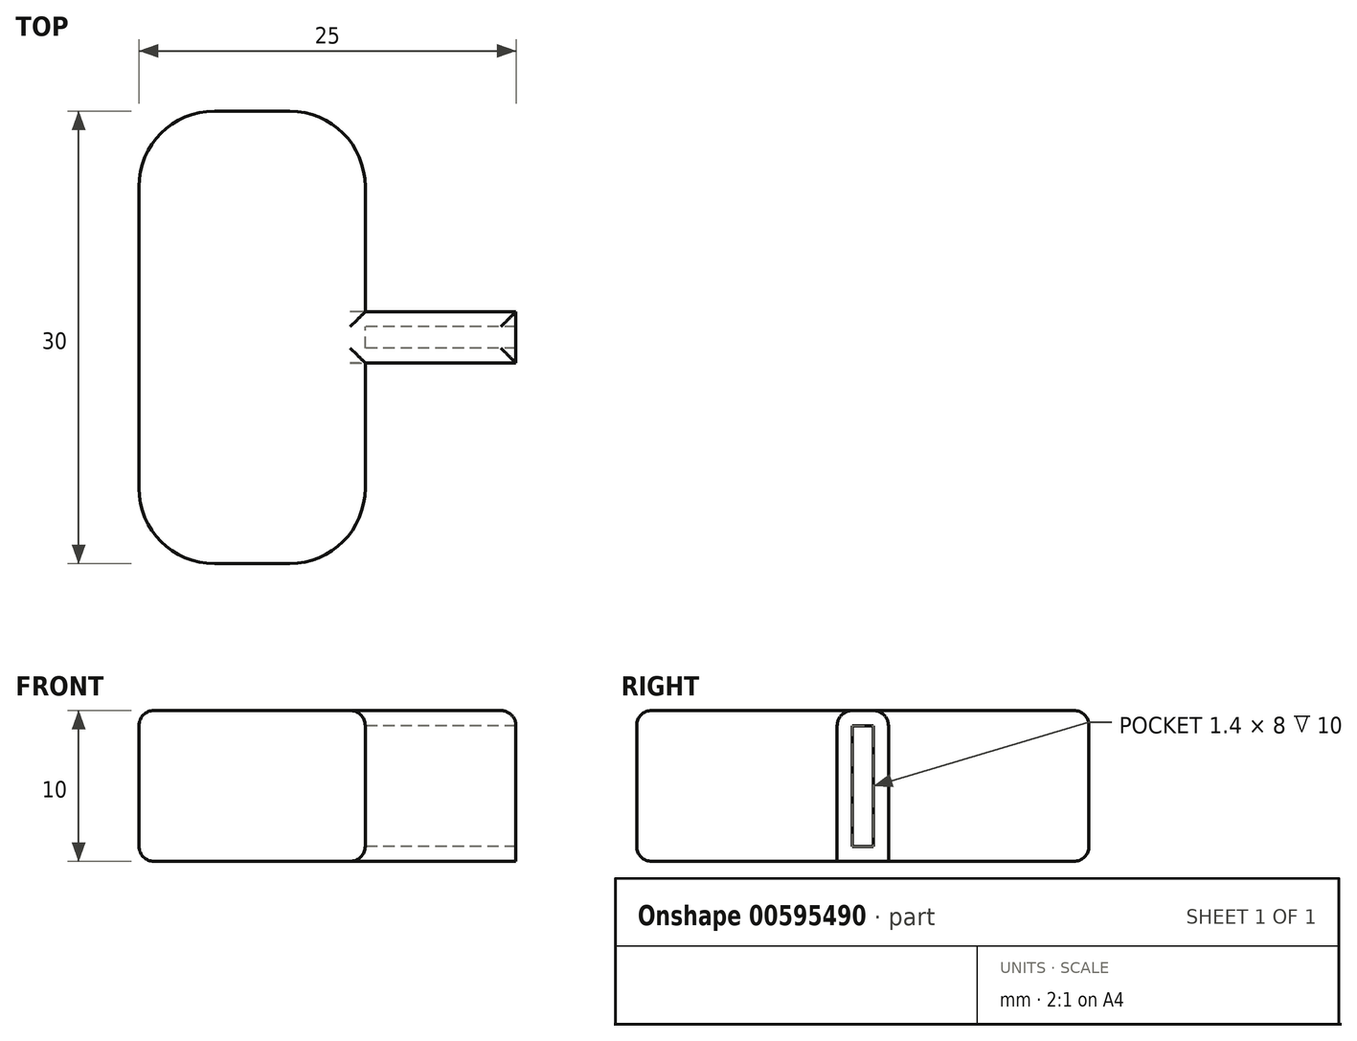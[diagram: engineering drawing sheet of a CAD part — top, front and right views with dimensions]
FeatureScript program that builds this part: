
annotation { "Feature Type Name" : "Feature", "Feature Type Description" : "" }
export const myFeature = defineFeature(function(context is Context, id is Id, definition is map)
    precondition{}
    {
        {
            var Q0;
            Q0=qCreatedBy(makeId("Top.planeOp"),FACE);
            var sketch = newSketch(context, id + "F0", { "sketchPlane" : qUnion([Q0])});
            skLineSegment(sketch, "E0.top", {"start": v(-33.1, 30) * mm, "end": v(-18.1, 30) * mm});
            skLineSegment(sketch, "E0.left", {"start": v(-33.1, 0) * mm, "end": v(-33.1, 30) * mm});
            skLineSegment(sketch, "E0.right", {"start": v(-18.1, 0) * mm, "end": v(-18.1, 30) * mm});
            skLineSegment(sketch, "E1", {"start": v(-33.1, 0) * mm, "end": v(-18.1, 0) * mm});
            skSolve(sketch);
        }
        {
            var Q0;
            Q0 = qSketchRegion(id + "F0", true);
            extrude(context, id + "F1", {"entities" : qUnion([Q0]), "depth" : 10 * mm, "offsetDistance" : 25 * mm});
        }
        {
            var Q0;
            Q0=makeQuery(id+"F1.opExtrude","SWEPT_FACE",FACE,{"disambiguationData":[OSD([sQuery(id+"F0.wireOp",EDGE,"E0.right")])]});
            var sketch = newSketch(context, id + "F2", { "sketchPlane" : qUnion([Q0])});
            skLineSegment(sketch, "E2", {"start": v(15.7, 9) * mm, "end": v(15.7, 1) * mm});
            skLineSegment(sketch, "E3", {"start": v(15.7, 1) * mm, "end": v(14.3, 1) * mm});
            skLineSegment(sketch, "E4", {"start": v(14.3, 1) * mm, "end": v(14.3, 9) * mm});
            skLineSegment(sketch, "E5", {"start": v(14.3, 9) * mm, "end": v(15.7, 9) * mm});
            skLineSegment(sketch, "E6.0", {"start": v(16.7, 10) * mm, "end": v(16.7, 0) * mm});
            skLineSegment(sketch, "E6.1", {"start": v(13.3, 10) * mm, "end": v(16.7, 10) * mm});
            skLineSegment(sketch, "E6.2", {"start": v(13.3, 0) * mm, "end": v(13.3, 10) * mm});
            skLineSegment(sketch, "E6.3", {"start": v(16.7, 0) * mm, "end": v(13.3, 0) * mm});
            skSolve(sketch);
        }
        {
            var Q0;
            Q0 = qSketchRegion(id + "F2", true);
            extrude(context, id + "F3", {"entities" : qUnion([Q0]), "operationType" : NewBodyOperationType.ADD, "depth" : 10 * mm, "offsetDistance" : 25 * mm});
        }
        {
            var Q0;
            Q0=makeQuery(id+"F1.opExtrude","SWEPT_EDGE",EDGE,{"disambiguationData":[OSD([sQuery(id+"F0.wireOp",EDGE,"E0.top"),sQuery(id+"F0.wireOp",EDGE,"E0.right")])]});
            var Q1;
            Q1=makeQuery(id+"F1.opExtrude","SWEPT_EDGE",EDGE,{"disambiguationData":[OSD([sQuery(id+"F0.wireOp",EDGE,"E0.top"),sQuery(id+"F0.wireOp",EDGE,"E0.left")])]});
            var Q2;
            Q2=makeQuery(id+"F1.opExtrude","SWEPT_EDGE",EDGE,{"disambiguationData":[OSD([sQuery(id+"F0.wireOp",EDGE,"E0.left"),sQuery(id+"F0.wireOp",EDGE,"E1")])]});
            var Q3;
            Q3=makeQuery(id+"F1.opExtrude","SWEPT_EDGE",EDGE,{"disambiguationData":[OSD([sQuery(id+"F0.wireOp",EDGE,"E0.right"),sQuery(id+"F0.wireOp",EDGE,"E1")])]});
            fillet(context, id + "F4", {"entities" : qUnion([Q0, Q1, Q2, Q3]), "radius" : 5 * mm, "tangentPropagation" : true, "allowEdgeOverflow" : false});
        }
        {
            var Q0;
            Q0=makeQuery(id+"F1.opExtrude","CAP_EDGE",EDGE,{"disambiguationData":[OSD([sQuery(id+"F0.wireOp",EDGE,"E0.left")])],"isStart":false});
            var Q1;
            {var subQ0=sQuery(id+"F0.wireOp",EDGE,"E0.left");var subQ1=sQuery(id+"F0.wireOp",EDGE,"E0.top");Q1=makeQuery(id+"F4.opFillet","BLEND_EDGE",EDGE,{"blendedFrom":[makeQuery(id+"F1.opExtrude","SWEPT_EDGE",EDGE,{"disambiguationData":[OSD([subQ1,subQ0])]}),makeQuery(id+"F1.opExtrude","CAP_FACE",FACE,{"disambiguationData":[OSD([subQ1,subQ0,sQuery(id+"F0.wireOp",EDGE,"E0.right"),sQuery(id+"F0.wireOp",EDGE,"E1")])],"isStart":false})],"blendedInto":[makeQuery(id+"F1.opExtrude","CAP_FACE",FACE,{"disambiguationData":[OSD([subQ1,subQ0,sQuery(id+"F0.wireOp",EDGE,"E0.right"),sQuery(id+"F0.wireOp",EDGE,"E1")])],"isStart":false})]});}
            var Q2;
            Q2=makeQuery(id+"F1.opExtrude","CAP_EDGE",EDGE,{"disambiguationData":[OSD([sQuery(id+"F0.wireOp",EDGE,"E0.top")])],"isStart":false});
            var Q3;
            {var subQ0=sQuery(id+"F0.wireOp",EDGE,"E0.right");var subQ1=sQuery(id+"F0.wireOp",EDGE,"E0.top");Q3=makeQuery(id+"F4.opFillet","BLEND_EDGE",EDGE,{"blendedFrom":[makeQuery(id+"F1.opExtrude","SWEPT_EDGE",EDGE,{"disambiguationData":[OSD([subQ1,subQ0])]}),makeQuery(id+"F1.opExtrude","CAP_FACE",FACE,{"disambiguationData":[OSD([subQ1,sQuery(id+"F0.wireOp",EDGE,"E0.left"),subQ0,sQuery(id+"F0.wireOp",EDGE,"E1")])],"isStart":false})],"blendedInto":[makeQuery(id+"F1.opExtrude","CAP_FACE",FACE,{"disambiguationData":[OSD([subQ1,sQuery(id+"F0.wireOp",EDGE,"E0.left"),subQ0,sQuery(id+"F0.wireOp",EDGE,"E1")])],"isStart":false})]});}
            var Q4;
            Q4=makeQuery(id+"F1.opExtrude","CAP_EDGE",EDGE,{"disambiguationData":[OSD([sQuery(id+"F0.wireOp",EDGE,"E0.right")])],"isStart":false});
            var Q5;
            {var subQ0=sQuery(id+"F0.wireOp",EDGE,"E1");var subQ1=sQuery(id+"F0.wireOp",EDGE,"E0.right");Q5=makeQuery(id+"F4.opFillet","BLEND_EDGE",EDGE,{"blendedFrom":[makeQuery(id+"F1.opExtrude","SWEPT_EDGE",EDGE,{"disambiguationData":[OSD([subQ1,subQ0])]}),makeQuery(id+"F1.opExtrude","CAP_FACE",FACE,{"disambiguationData":[OSD([sQuery(id+"F0.wireOp",EDGE,"E0.top"),sQuery(id+"F0.wireOp",EDGE,"E0.left"),subQ1,subQ0])],"isStart":false})],"blendedInto":[makeQuery(id+"F1.opExtrude","CAP_FACE",FACE,{"disambiguationData":[OSD([sQuery(id+"F0.wireOp",EDGE,"E0.top"),sQuery(id+"F0.wireOp",EDGE,"E0.left"),subQ1,subQ0])],"isStart":false})]});}
            var Q6;
            Q6=makeQuery(id+"F1.opExtrude","CAP_EDGE",EDGE,{"disambiguationData":[OSD([sQuery(id+"F0.wireOp",EDGE,"E1")])],"isStart":false});
            var Q7;
            {var subQ0=sQuery(id+"F0.wireOp",EDGE,"E1");var subQ1=sQuery(id+"F0.wireOp",EDGE,"E0.left");Q7=makeQuery(id+"F4.opFillet","BLEND_EDGE",EDGE,{"blendedFrom":[makeQuery(id+"F1.opExtrude","SWEPT_EDGE",EDGE,{"disambiguationData":[OSD([subQ1,subQ0])]}),makeQuery(id+"F1.opExtrude","CAP_FACE",FACE,{"disambiguationData":[OSD([sQuery(id+"F0.wireOp",EDGE,"E0.top"),subQ1,sQuery(id+"F0.wireOp",EDGE,"E0.right"),subQ0])],"isStart":false})],"blendedInto":[makeQuery(id+"F1.opExtrude","CAP_FACE",FACE,{"disambiguationData":[OSD([sQuery(id+"F0.wireOp",EDGE,"E0.top"),subQ1,sQuery(id+"F0.wireOp",EDGE,"E0.right"),subQ0])],"isStart":false})]});}
            fillet(context, id + "F5", {"entities" : qUnion([Q0, Q1, Q2, Q3, Q4, Q5, Q6, Q7]), "radius" : 1 * mm, "tangentPropagation" : true, "allowEdgeOverflow" : false});
        }
        {
            var Q0;
            Q0=makeQuery(id+"F1.opExtrude","CAP_EDGE",EDGE,{"disambiguationData":[OSD([sQuery(id+"F0.wireOp",EDGE,"E0.right")])],"isStart":true});
            var Q1;
            {var subQ0=sQuery(id+"F0.wireOp",EDGE,"E1");var subQ1=sQuery(id+"F0.wireOp",EDGE,"E0.right");Q1=makeQuery(id+"F4.opFillet","BLEND_EDGE",EDGE,{"blendedFrom":[makeQuery(id+"F1.opExtrude","SWEPT_EDGE",EDGE,{"disambiguationData":[OSD([subQ1,subQ0])]}),makeQuery(id+"F1.opExtrude","CAP_FACE",FACE,{"disambiguationData":[OSD([sQuery(id+"F0.wireOp",EDGE,"E0.top"),sQuery(id+"F0.wireOp",EDGE,"E0.left"),subQ1,subQ0])],"isStart":true})],"blendedInto":[makeQuery(id+"F1.opExtrude","CAP_FACE",FACE,{"disambiguationData":[OSD([sQuery(id+"F0.wireOp",EDGE,"E0.top"),sQuery(id+"F0.wireOp",EDGE,"E0.left"),subQ1,subQ0])],"isStart":true})]});}
            var Q2;
            Q2=makeQuery(id+"F1.opExtrude","CAP_EDGE",EDGE,{"disambiguationData":[OSD([sQuery(id+"F0.wireOp",EDGE,"E1")])],"isStart":true});
            var Q3;
            {var subQ0=sQuery(id+"F0.wireOp",EDGE,"E1");var subQ1=sQuery(id+"F0.wireOp",EDGE,"E0.left");Q3=makeQuery(id+"F4.opFillet","BLEND_EDGE",EDGE,{"blendedFrom":[makeQuery(id+"F1.opExtrude","SWEPT_EDGE",EDGE,{"disambiguationData":[OSD([subQ1,subQ0])]}),makeQuery(id+"F1.opExtrude","CAP_FACE",FACE,{"disambiguationData":[OSD([sQuery(id+"F0.wireOp",EDGE,"E0.top"),subQ1,sQuery(id+"F0.wireOp",EDGE,"E0.right"),subQ0])],"isStart":true})],"blendedInto":[makeQuery(id+"F1.opExtrude","CAP_FACE",FACE,{"disambiguationData":[OSD([sQuery(id+"F0.wireOp",EDGE,"E0.top"),subQ1,sQuery(id+"F0.wireOp",EDGE,"E0.right"),subQ0])],"isStart":true})]});}
            var Q4;
            Q4=makeQuery(id+"F1.opExtrude","CAP_EDGE",EDGE,{"disambiguationData":[OSD([sQuery(id+"F0.wireOp",EDGE,"E0.left")])],"isStart":true});
            var Q5;
            {var subQ0=sQuery(id+"F0.wireOp",EDGE,"E0.left");var subQ1=sQuery(id+"F0.wireOp",EDGE,"E0.top");Q5=makeQuery(id+"F4.opFillet","BLEND_EDGE",EDGE,{"blendedFrom":[makeQuery(id+"F1.opExtrude","SWEPT_EDGE",EDGE,{"disambiguationData":[OSD([subQ1,subQ0])]}),makeQuery(id+"F1.opExtrude","CAP_FACE",FACE,{"disambiguationData":[OSD([subQ1,subQ0,sQuery(id+"F0.wireOp",EDGE,"E0.right"),sQuery(id+"F0.wireOp",EDGE,"E1")])],"isStart":true})],"blendedInto":[makeQuery(id+"F1.opExtrude","CAP_FACE",FACE,{"disambiguationData":[OSD([subQ1,subQ0,sQuery(id+"F0.wireOp",EDGE,"E0.right"),sQuery(id+"F0.wireOp",EDGE,"E1")])],"isStart":true})]});}
            var Q6;
            Q6=makeQuery(id+"F1.opExtrude","CAP_EDGE",EDGE,{"disambiguationData":[OSD([sQuery(id+"F0.wireOp",EDGE,"E0.top")])],"isStart":true});
            var Q7;
            {var subQ0=sQuery(id+"F0.wireOp",EDGE,"E0.right");var subQ1=sQuery(id+"F0.wireOp",EDGE,"E0.top");Q7=makeQuery(id+"F4.opFillet","BLEND_EDGE",EDGE,{"blendedFrom":[makeQuery(id+"F1.opExtrude","SWEPT_EDGE",EDGE,{"disambiguationData":[OSD([subQ1,subQ0])]}),makeQuery(id+"F1.opExtrude","CAP_FACE",FACE,{"disambiguationData":[OSD([subQ1,sQuery(id+"F0.wireOp",EDGE,"E0.left"),subQ0,sQuery(id+"F0.wireOp",EDGE,"E1")])],"isStart":true})],"blendedInto":[makeQuery(id+"F1.opExtrude","CAP_FACE",FACE,{"disambiguationData":[OSD([subQ1,sQuery(id+"F0.wireOp",EDGE,"E0.left"),subQ0,sQuery(id+"F0.wireOp",EDGE,"E1")])],"isStart":true})]});}
            var Q8;
            Q8=makeQuery(id+"F1.opExtrude","CAP_FACE",FACE,{"disambiguationData":[OSD([sQuery(id+"F0.wireOp",EDGE,"E0.top"),sQuery(id+"F0.wireOp",EDGE,"E0.left"),sQuery(id+"F0.wireOp",EDGE,"E0.right"),sQuery(id+"F0.wireOp",EDGE,"E1")])],"isStart":false});
            fillet(context, id + "F6", {"entities" : qUnion([Q0, Q1, Q2, Q3, Q4, Q5, Q6, Q7, Q8]), "radius" : 1 * mm, "tangentPropagation" : true, "allowEdgeOverflow" : false});
        }
    });
